MODEL slx_cde280f26b68
KIND model
CONFIG AbsTol = auto
CONFIG EnableMultiTasking = off
CONFIG FixedStep = auto
CONFIG MaxStep = auto
CONFIG MinStep = auto
CONFIG RelTol = 1e-3
CONFIG SampleTimeConstraint = Unconstrained
CONFIG Solver = VariableStepAuto
CONFIG SolverName = VariableStepAuto
CONFIG StartTime = 0.0
CONFIG StopTime = 30
BLOCK [Gain] Controller
  Gain = K
  OutDataTypeStr = Inherit: Inherit via internal rule
  ParamDataTypeStr = Inherit: Inherit via internal rule
  SaturateOnIntegerOverflow = off
BLOCK [Scope] Scope
  NumInputPorts = 1
  Ports = [1]
  ScopeSpecificationString = Simulink.scopes.TimeScopeBlockCfg('CurrentConfiguration', extmgr.ConfigurationSet(extmgr.Configuration('Core','General UI',true),extmgr.Configuration('Core','Source UI',true),extmgr.Configuration('Sources','WiredSimulink',true),extmgr.Configuration('Visuals','Time Domain',true,'SerializedDisplays',{struct('MinYLimReal','-0.14049','MaxYLimReal','1.2644','YLabelReal','','MinYLimMag','0.00000','MaxYL...<+1358ch>
BLOCK [Step] Step
  SampleTime = 0
BLOCK [Sum] Sum
  IconShape = round
  InputSameDT = off
  Inputs = |+-
  OutDataTypeStr = Inherit: Inherit via internal rule
  Ports = [2, 1]
  SaturateOnIntegerOverflow = off
BLOCK [TransferFcn] Transfer Fcn
  Denominator = den
  Numerator = num
ANNOTATION (root): Christopher Lum <email> This accompanies the YouTube video located at https://youtu.be/rNYHww84juM Version History: 1/20/18: Created
LINE Controller:1 -> Transfer Fcn:1
LINE Step:1 -> Sum:1
LINE Sum:1 -> Controller:1
NET Transfer Fcn:1 -> Scope:1, Sum:2
note: NET lines group one-source signal fan-out (src -> all destinations, sorted); 1:1 wires keep LINE
